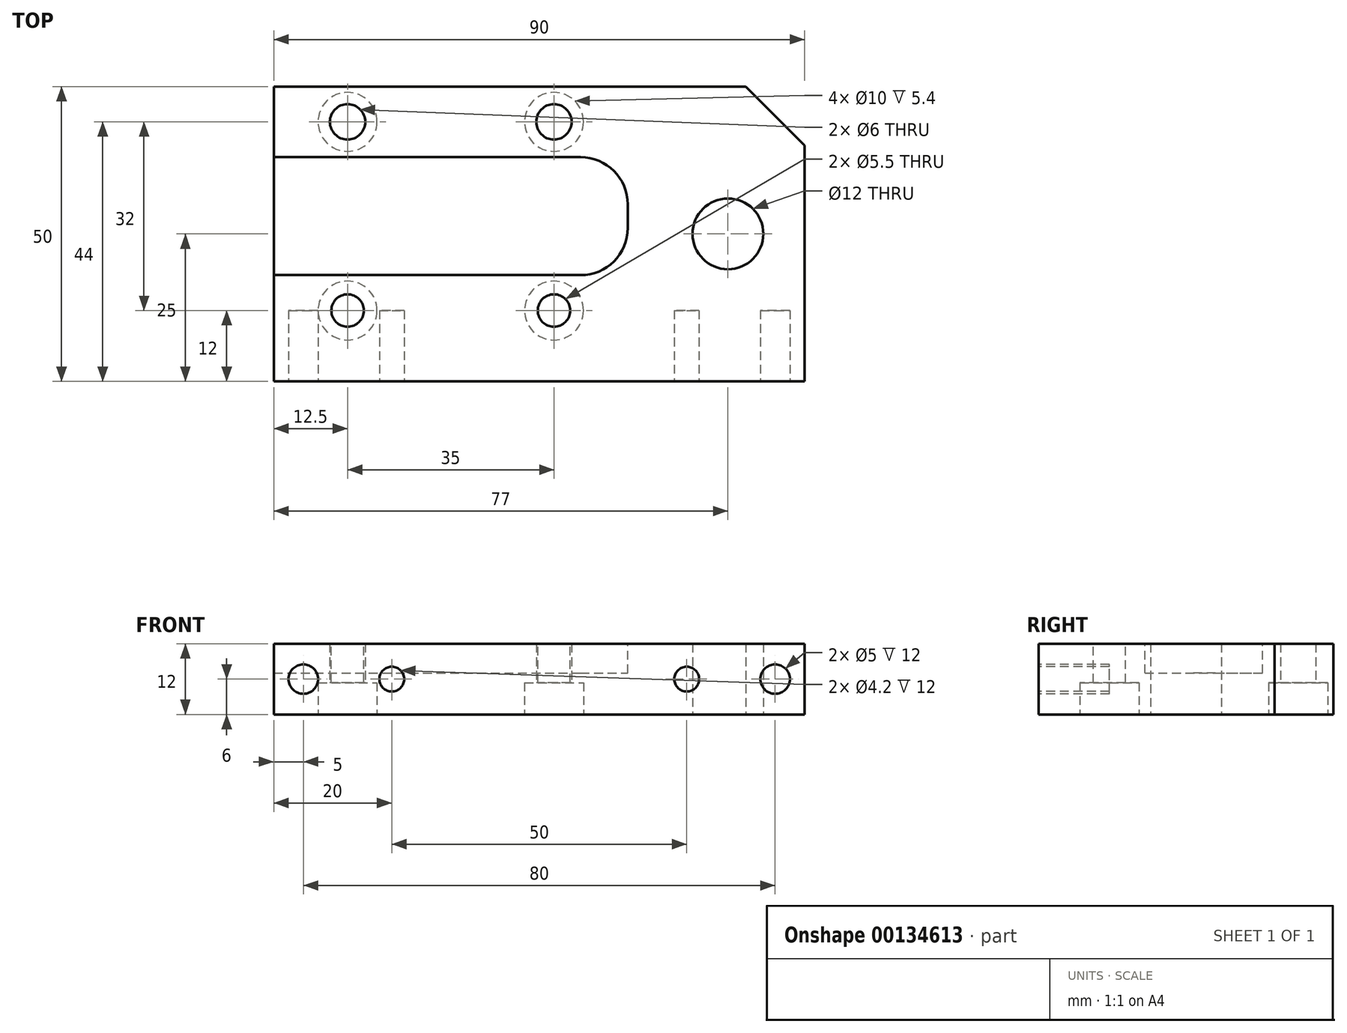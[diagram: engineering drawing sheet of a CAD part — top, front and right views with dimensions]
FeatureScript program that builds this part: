
annotation { "Feature Type Name" : "Feature", "Feature Type Description" : "" }
export const myFeature = defineFeature(function(context is Context, id is Id, definition is map)
    precondition{}
    {
        {
            var Q0;
            Q0=qCreatedBy(makeId("Top.planeOp"),FACE);
            var sketch = newSketch(context, id + "F0", { "sketchPlane" : qUnion([Q0])});
            skLineSegment(sketch, "E0.bottom", {"start": v(45, -25) * mm, "end": v(-45, -25) * mm});
            skLineSegment(sketch, "E0.top", {"start": v(35, 25) * mm, "end": v(-45, 25) * mm});
            skLineSegment(sketch, "E0.left", {"start": v(45, -25) * mm, "end": v(45, 15) * mm});
            skLineSegment(sketch, "E0.right", {"start": v(-45, -25) * mm, "end": v(-45, 25) * mm});
            skPoint(sketch, "E0.middle", {"position": v(0, 0) * mm});
            skLineSegment(sketch, "E1.bottom", {"start": v(-45, 13) * mm, "end": v(7, 13) * mm});
            skLineSegment(sketch, "E1.top", {"start": v(-45, -7) * mm, "end": v(7, -7) * mm});
            skLineSegment(sketch, "E1.left", {"start": v(-45, 13) * mm, "end": v(-45, -7) * mm});
            skLineSegment(sketch, "E1.right", {"start": v(15, 5) * mm, "end": v(15, 1) * mm});
            skPoint(sketch, "E2", {"position": v(15, 3) * mm});
            skPoint(sketch, "E3.visualSharp", {"position": v(15, 13) * mm});
            skArc(sketch, "E3.filletArc", {"start": v(15, 5) * mm, "mid": v(12.66, 10.66) * mm, "end": v(7, 13) * mm});
            skPoint(sketch, "E4.visualSharp", {"position": v(15, -7) * mm});
            skArc(sketch, "E4.filletArc", {"start": v(7, -7) * mm, "mid": v(12.66, -4.66) * mm, "end": v(15, 1) * mm});
            skCircle(sketch, "E5", {"center": v(32, 0) * mm, "radius": 6 * mm});
            skLineSegment(sketch, "E6", {"start": v(35, 25) * mm, "end": v(45, 15) * mm});
            skPoint(sketch, "E7.orphan", {"position": v(45, 25) * mm});
            skCircle(sketch, "E8", {"center": v(-32.5, 19) * mm, "radius": 3 * mm});
            skCircle(sketch, "E9", {"center": v(2.5, 19) * mm, "radius": 3 * mm});
            skSolve(sketch);
        }
        {
            var Q0;
            {var subQ5=sQuery(id+"F0.wireOp",EDGE,"E0.bottom");Q0=makeQuery(id+"F0.imprint","IMPRINT",FACE,{"disambiguationData":[TD([[makeQuery(id+"F0.imprint","IMPRINT",EDGE,{"derivedFrom":subQ5}),-1.0]])]});}
            var Q1;
            Q1=makeQuery(id+"F0.imprint","IMPRINT",FACE,{"disambiguationData":[TD([[makeQuery(id+"F0.imprint","IMPRINT",EDGE,{"derivedFrom":sQuery(id+"F0.wireOp",EDGE,"E1.bottom")}),-1.0]])]});
            extrude(context, id + "F1", {"entities" : qUnion([Q0, Q1]), "depth" : 12 * mm});
        }
        {
            var Q0;
            Q0=makeQuery(id+"F1.opExtrude","CAP_FACE",FACE,{"disambiguationData":[OSD([sQuery(id+"F0.wireOp",EDGE,"E0.bottom"),sQuery(id+"F0.wireOp",EDGE,"E0.top"),sQuery(id+"F0.wireOp",EDGE,"E0.left"),sQuery(id+"F0.wireOp",EDGE,"E0.right"),sQuery(id+"F0.wireOp",EDGE,"E1.left"),sQuery(id+"F0.wireOp",EDGE,"E6"),sQuery(id+"F0.wireOp",EDGE,"E8"),sQuery(id+"F0.wireOp",EDGE,"E9")])],"isStart":false});
            var sketch = newSketch(context, id + "F2", { "sketchPlane" : qUnion([Q0])});
            skLineSegment(sketch, "E10.bottom", {"start": v(45, -25) * mm, "end": v(-45, -25) * mm});
            skLineSegment(sketch, "E10.top", {"start": v(35, 25) * mm, "end": v(-45, 25) * mm});
            skLineSegment(sketch, "E10.left", {"start": v(45, -25) * mm, "end": v(45, 15) * mm});
            skLineSegment(sketch, "E10.right", {"start": v(-45, -25) * mm, "end": v(-45, 25) * mm});
            skPoint(sketch, "E10.middle", {"position": v(0, 0) * mm});
            skLineSegment(sketch, "E11.bottom", {"start": v(-45, 13) * mm, "end": v(7, 13) * mm});
            skLineSegment(sketch, "E11.top", {"start": v(-45, -7) * mm, "end": v(7, -7) * mm});
            skLineSegment(sketch, "E11.left", {"start": v(-45, 13) * mm, "end": v(-45, -7) * mm});
            skLineSegment(sketch, "E11.right", {"start": v(15, 5) * mm, "end": v(15, 1) * mm});
            skPoint(sketch, "E12", {"position": v(15, 3) * mm});
            skPoint(sketch, "E13.visualSharp", {"position": v(15, 13) * mm});
            skArc(sketch, "E13.filletArc", {"start": v(15, 5) * mm, "mid": v(12.66, 10.66) * mm, "end": v(7, 13) * mm});
            skPoint(sketch, "E14.visualSharp", {"position": v(15, -7) * mm});
            skArc(sketch, "E14.filletArc", {"start": v(7, -7) * mm, "mid": v(12.66, -4.66) * mm, "end": v(15, 1) * mm});
            skCircle(sketch, "E15", {"center": v(32, 3) * mm, "radius": 6 * mm});
            skLineSegment(sketch, "E16", {"start": v(35, 25) * mm, "end": v(45, 15) * mm});
            skPoint(sketch, "E17.orphan", {"position": v(45, 25) * mm});
            skCircle(sketch, "E18", {"center": v(-32.5, 19) * mm, "radius": 3 * mm});
            skCircle(sketch, "E19", {"center": v(2.5, 19) * mm, "radius": 3 * mm});
            skSolve(sketch);
        }
        {
            var Q0;
            Q0=makeQuery(id+"F2.imprint","IMPRINT",FACE,{"disambiguationData":[TD([[makeQuery(id+"F2.imprint","IMPRINT",EDGE,{"derivedFrom":sQuery(id+"F2.wireOp",EDGE,"E11.bottom")}),-1.0]])]});
            extrude(context, id + "F3", {"entities" : qUnion([Q0]), "operationType" : NewBodyOperationType.REMOVE, "oppositeDirection" : true, "depth" : (12 - 7) * mm});
        }
        {
            var Q0;
            Q0=makeQuery(id+"F1.opExtrude","CAP_FACE",FACE,{"disambiguationData":[OSD([sQuery(id+"F0.wireOp",EDGE,"E0.bottom"),sQuery(id+"F0.wireOp",EDGE,"E0.top"),sQuery(id+"F0.wireOp",EDGE,"E0.left"),sQuery(id+"F0.wireOp",EDGE,"E0.right"),sQuery(id+"F0.wireOp",EDGE,"E1.left"),sQuery(id+"F0.wireOp",EDGE,"E6"),sQuery(id+"F0.wireOp",EDGE,"E8"),sQuery(id+"F0.wireOp",EDGE,"E9")])],"isStart":false});
            var sketch = newSketch(context, id + "F4", { "sketchPlane" : qUnion([Q0])});
            skCircle(sketch, "E20.0", {"center": v(-32.5, 19) * mm, "radius": 3 * mm});
            skCircle(sketch, "E21.0", {"center": v(2.5, 19) * mm, "radius": 3 * mm});
            skCircle(sketch, "E22", {"center": v(-32.5, -13) * mm, "radius": 2.75 * mm});
            skCircle(sketch, "E23", {"center": v(2.5, -13) * mm, "radius": 2.75 * mm});
            skSolve(sketch);
        }
        {
            var Q0;
            Q0=makeQuery(id+"F4.imprint","IMPRINT",FACE,{"disambiguationData":[TD([[makeQuery(id+"F4.imprint","IMPRINT",EDGE,{"derivedFrom":sQuery(id+"F4.wireOp",EDGE,"E22")}),1.0]])]});
            var Q1;
            Q1=makeQuery(id+"F4.imprint","IMPRINT",FACE,{"disambiguationData":[TD([[makeQuery(id+"F4.imprint","IMPRINT",EDGE,{"derivedFrom":sQuery(id+"F4.wireOp",EDGE,"E23")}),1.0]])]});
            extrude(context, id + "F5", {"entities" : qUnion([Q0, Q1]), "operationType" : NewBodyOperationType.REMOVE, "oppositeDirection" : true, "depth" : 25 * mm});
        }
        {
            var Q0;
            Q0=makeQuery(id+"F1.opExtrude","SWEPT_FACE",FACE,{"disambiguationData":[OSD([sQuery(id+"F0.wireOp",EDGE,"E0.bottom")])]});
            var sketch = newSketch(context, id + "F6", { "sketchPlane" : qUnion([Q0])});
            skCircle(sketch, "E24", {"center": v(-40, 6) * mm, "radius": 2.5 * mm});
            skCircle(sketch, "E25", {"center": v(-25, 6) * mm, "radius": 2.1 * mm});
            skCircle(sketch, "E26", {"center": v(25, 6) * mm, "radius": 2.1 * mm});
            skCircle(sketch, "E27", {"center": v(40, 6) * mm, "radius": 2.5 * mm});
            skLineSegment(sketch, "E28", {"start": v(0, 0) * mm, "end": v(0, 12) * mm});
            skPoint(sketch, "E29", {"position": v(-45, 6) * mm});
            skSolve(sketch);
        }
        {
            var Q0;
            Q0=makeQuery(id+"F6.imprint","IMPRINT",FACE,{"disambiguationData":[TD([[makeQuery(id+"F6.imprint","IMPRINT",EDGE,{"derivedFrom":sQuery(id+"F6.wireOp",EDGE,"E24")}),1.0]])]});
            var Q1;
            Q1=makeQuery(id+"F6.imprint","IMPRINT",FACE,{"disambiguationData":[TD([[makeQuery(id+"F6.imprint","IMPRINT",EDGE,{"derivedFrom":sQuery(id+"F6.wireOp",EDGE,"E25")}),1.0]])]});
            var Q2;
            Q2=makeQuery(id+"F6.imprint","IMPRINT",FACE,{"disambiguationData":[TD([[makeQuery(id+"F6.imprint","IMPRINT",EDGE,{"derivedFrom":sQuery(id+"F6.wireOp",EDGE,"E26")}),1.0]])]});
            var Q3;
            Q3=makeQuery(id+"F6.imprint","IMPRINT",FACE,{"disambiguationData":[TD([[makeQuery(id+"F6.imprint","IMPRINT",EDGE,{"derivedFrom":sQuery(id+"F6.wireOp",EDGE,"E27")}),1.0]])]});
            extrude(context, id + "F7", {"entities" : qUnion([Q0, Q1, Q2, Q3]), "operationType" : NewBodyOperationType.REMOVE, "oppositeDirection" : true, "depth" : 12 * mm});
        }
        {
            var Q0;
            Q0=makeQuery(id+"F1.opExtrude","CAP_FACE",FACE,{"disambiguationData":[OSD([sQuery(id+"F0.wireOp",EDGE,"E0.bottom"),sQuery(id+"F0.wireOp",EDGE,"E0.top"),sQuery(id+"F0.wireOp",EDGE,"E0.left"),sQuery(id+"F0.wireOp",EDGE,"E0.right"),sQuery(id+"F0.wireOp",EDGE,"E1.left"),sQuery(id+"F0.wireOp",EDGE,"E5"),sQuery(id+"F0.wireOp",EDGE,"E6"),sQuery(id+"F0.wireOp",EDGE,"E8"),sQuery(id+"F0.wireOp",EDGE,"E9")])],"isStart":true});
            var sketch = newSketch(context, id + "F8", { "sketchPlane" : qUnion([Q0])});
            skCircle(sketch, "E30", {"center": v(2.5, -19) * mm, "radius": 5 * mm});
            skCircle(sketch, "E31", {"center": v(2.5, 13) * mm, "radius": 5 * mm});
            skCircle(sketch, "E32", {"center": v(-32.5, 13) * mm, "radius": 5 * mm});
            skCircle(sketch, "E33", {"center": v(-32.5, -19) * mm, "radius": 5 * mm});
            skSolve(sketch);
        }
        {
            var Q0;
            Q0=makeQuery(id+"F8.imprint","IMPRINT",FACE,{"disambiguationData":[TD([[makeQuery(id+"F8.imprint","IMPRINT",EDGE,{"derivedFrom":sQuery(id+"F8.wireOp",EDGE,"E30")}),1.0]])]});
            var Q1;
            Q1=makeQuery(id+"F8.imprint","IMPRINT",FACE,{"disambiguationData":[TD([[makeQuery(id+"F8.imprint","IMPRINT",EDGE,{"derivedFrom":sQuery(id+"F8.wireOp",EDGE,"E31")}),1.0]])]});
            var Q2;
            Q2=makeQuery(id+"F8.imprint","IMPRINT",FACE,{"disambiguationData":[TD([[makeQuery(id+"F8.imprint","IMPRINT",EDGE,{"derivedFrom":sQuery(id+"F8.wireOp",EDGE,"E33")}),1.0]])]});
            var Q3;
            Q3=makeQuery(id+"F8.imprint","IMPRINT",FACE,{"disambiguationData":[TD([[makeQuery(id+"F8.imprint","IMPRINT",EDGE,{"derivedFrom":sQuery(id+"F8.wireOp",EDGE,"E32")}),1.0]])]});
            extrude(context, id + "F9", {"entities" : qUnion([Q0, Q1, Q2, Q3]), "operationType" : NewBodyOperationType.REMOVE, "oppositeDirection" : true, "depth" : 5.4 * mm});
        }
    });
